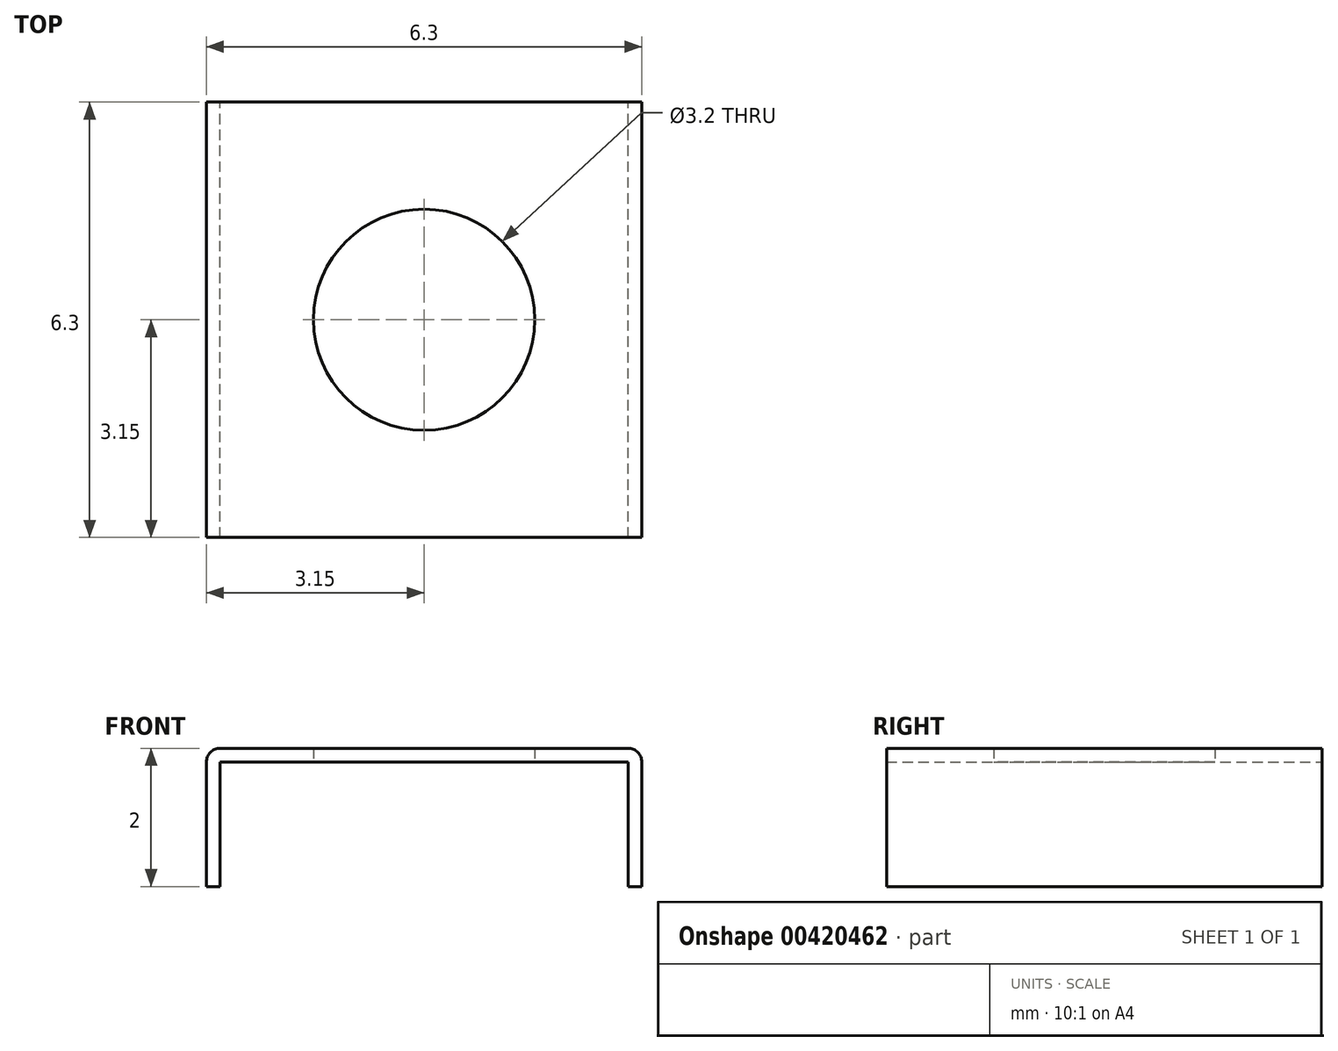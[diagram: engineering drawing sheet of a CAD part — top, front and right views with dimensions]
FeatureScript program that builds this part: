
annotation { "Feature Type Name" : "Feature", "Feature Type Description" : "" }
export const myFeature = defineFeature(function(context is Context, id is Id, definition is map)
    precondition{}
    {
        {
            var Q0;
            Q0=qCreatedBy(makeId("Top.planeOp"),FACE);
            var sketch = newSketch(context, id + "F0", { "sketchPlane" : qUnion([Q0])});
            skLineSegment(sketch, "E0.bottom", {"start": v(0, 0) * mm, "end": v(6.3, 0) * mm});
            skLineSegment(sketch, "E0.top", {"start": v(0, 6.3) * mm, "end": v(6.3, 6.3) * mm});
            skLineSegment(sketch, "E0.left", {"start": v(0, 0) * mm, "end": v(0, 6.3) * mm});
            skLineSegment(sketch, "E0.right", {"start": v(6.3, 0) * mm, "end": v(6.3, 6.3) * mm});
            skCircle(sketch, "E1", {"center": v(3.15, 3.15) * mm, "radius": 1.6 * mm});
            skSolve(sketch);
        }
        {
            var Q0;
            Q0 = qSketchRegion(id + "F0", true);
            extrude(context, id + "F1", {"entities" : qUnion([Q0]), "depth" : 0.2 * mm});
        }
        {
            var Q0;
            Q0=makeQuery(id+"F1.opExtrude","CAP_FACE",FACE,{"disambiguationData":[OSD([sQuery(id+"F0.wireOp",EDGE,"E0.bottom"),sQuery(id+"F0.wireOp",EDGE,"E0.top"),sQuery(id+"F0.wireOp",EDGE,"E0.left"),sQuery(id+"F0.wireOp",EDGE,"E0.right"),sQuery(id+"F0.wireOp",EDGE,"E1")])],"isStart":true});
            var sketch = newSketch(context, id + "F2", { "sketchPlane" : qUnion([Q0])});
            skLineSegment(sketch, "E2.bottom", {"start": v(0, 0) * mm, "end": v(0.2, 0) * mm});
            skLineSegment(sketch, "E2.top", {"start": v(0, -6.3) * mm, "end": v(0.2, -6.3) * mm});
            skLineSegment(sketch, "E2.left", {"start": v(0, 0) * mm, "end": v(0, -6.3) * mm});
            skLineSegment(sketch, "E2.right", {"start": v(0.2, 0) * mm, "end": v(0.2, -6.3) * mm});
            skLineSegment(sketch, "E3.bottom", {"start": v(6.3, 0) * mm, "end": v(6.1, 0) * mm});
            skLineSegment(sketch, "E3.top", {"start": v(6.3, -6.3) * mm, "end": v(6.1, -6.3) * mm});
            skLineSegment(sketch, "E3.left", {"start": v(6.3, 0) * mm, "end": v(6.3, -6.3) * mm});
            skLineSegment(sketch, "E3.right", {"start": v(6.1, 0) * mm, "end": v(6.1, -6.3) * mm});
            skSolve(sketch);
        }
        {
            var Q0;
            Q0 = qSketchRegion(id + "F2", true);
            extrude(context, id + "F3", {"entities" : qUnion([Q0]), "operationType" : NewBodyOperationType.ADD, "depth" : 1.8 * mm});
        }
        {
            var Q0;
            Q0=makeQuery(id+"F1.opExtrude","CAP_EDGE",EDGE,{"disambiguationData":[OSD([sQuery(id+"F0.wireOp",EDGE,"E0.left")])],"isStart":false});
            var Q1;
            Q1=makeQuery(id+"F1.opExtrude","CAP_EDGE",EDGE,{"disambiguationData":[OSD([sQuery(id+"F0.wireOp",EDGE,"E0.right")])],"isStart":false});
            fillet(context, id + "F4", {"entities" : qUnion([Q0, Q1]), "radius" : 0.2 * mm, "tangentPropagation" : true, "allowEdgeOverflow" : false});
        }
    });
